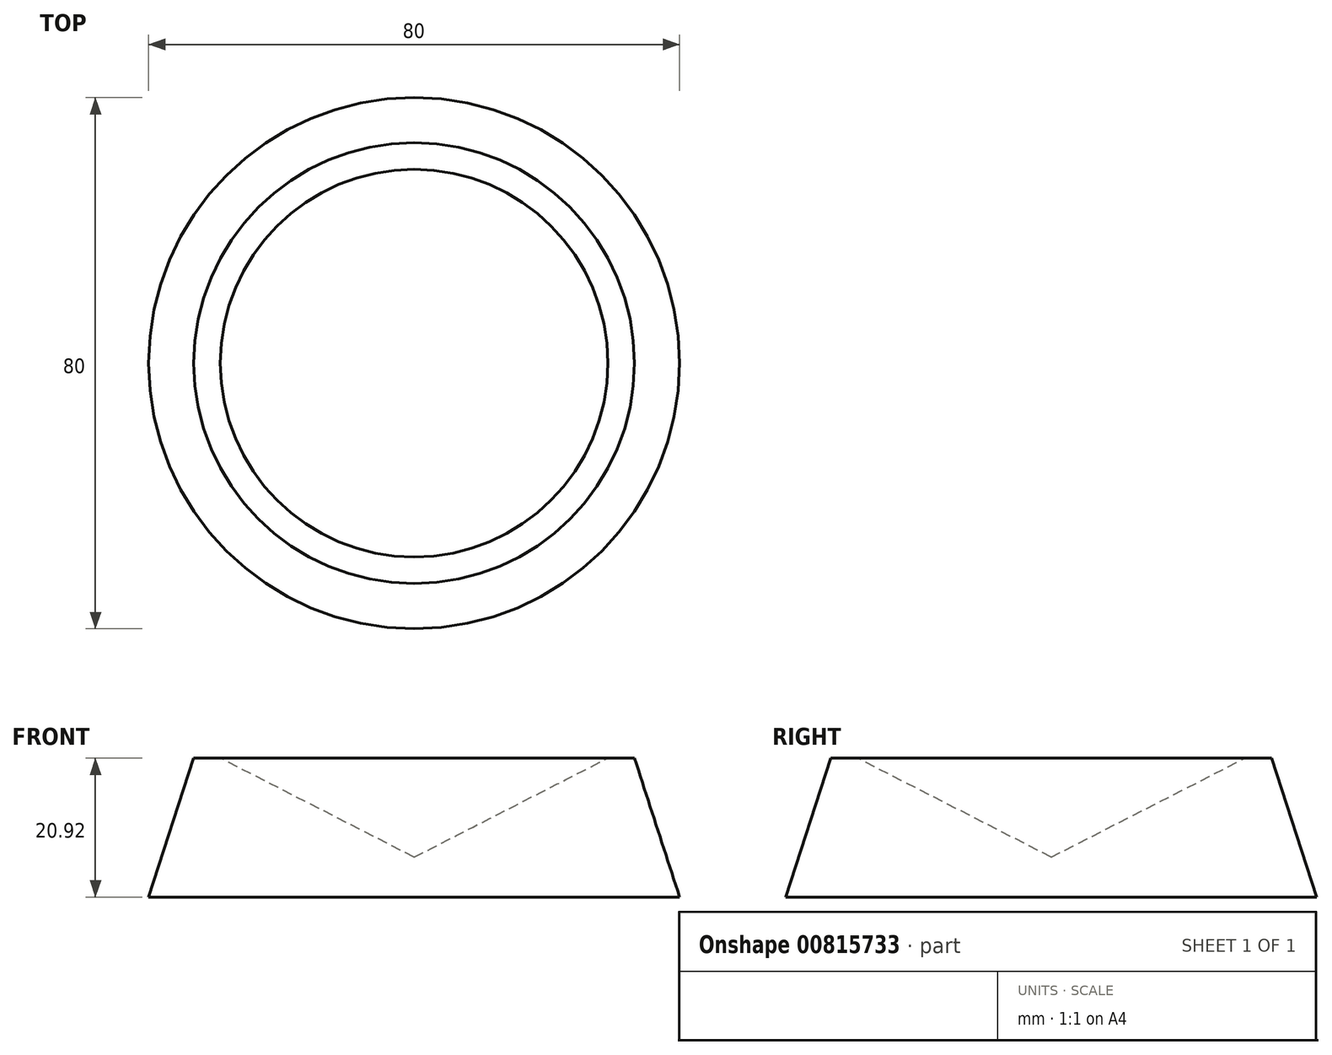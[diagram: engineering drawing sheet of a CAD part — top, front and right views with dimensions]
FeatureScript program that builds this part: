
annotation { "Feature Type Name" : "Feature", "Feature Type Description" : "" }
export const myFeature = defineFeature(function(context is Context, id is Id, definition is map)
    precondition{}
    {
        {
            var Q0;
            Q0=qCreatedBy(makeId("Front.planeOp"),FACE);
            var sketch = newSketch(context, id + "F0", { "sketchPlane" : qUnion([Q0])});
            skLineSegment(sketch, "E0", {"start": v(0, 0) * mm, "end": v(40, 0) * mm});
            skLineSegment(sketch, "E1", {"start": v(40, 0) * mm, "end": v(33.2, 20.92) * mm});
            skLineSegment(sketch, "E2", {"start": v(33.2, 20.92) * mm, "end": v(29.2, 20.92) * mm});
            skLineSegment(sketch, "E3", {"start": v(29.2, 20.92) * mm, "end": v(0, 6) * mm});
            skLineSegment(sketch, "E4", {"start": v(0, 6) * mm, "end": v(0, 0) * mm});
            skSolve(sketch);
        }
        {
            var Q0;
            Q0=makeQuery(id+"F0.imprint","IMPRINT",FACE,{"disambiguationData":[TD([[makeQuery(id+"F0.imprint","IMPRINT",EDGE,{"derivedFrom":sQuery(id+"F0.wireOp",EDGE,"E0")}),1.0]])]});
            var Q1;
            Q1=sQuery(id+"F0.wireOp",EDGE,"E4");
            revolve(context, id + "F1", {"surfaceOperationType" : NewSurfaceOperationType.NEW, "entities" : qUnion([Q0]), "axis" : qUnion([Q1]), "revolveType" : RevolveType.FULL});
        }
    });
